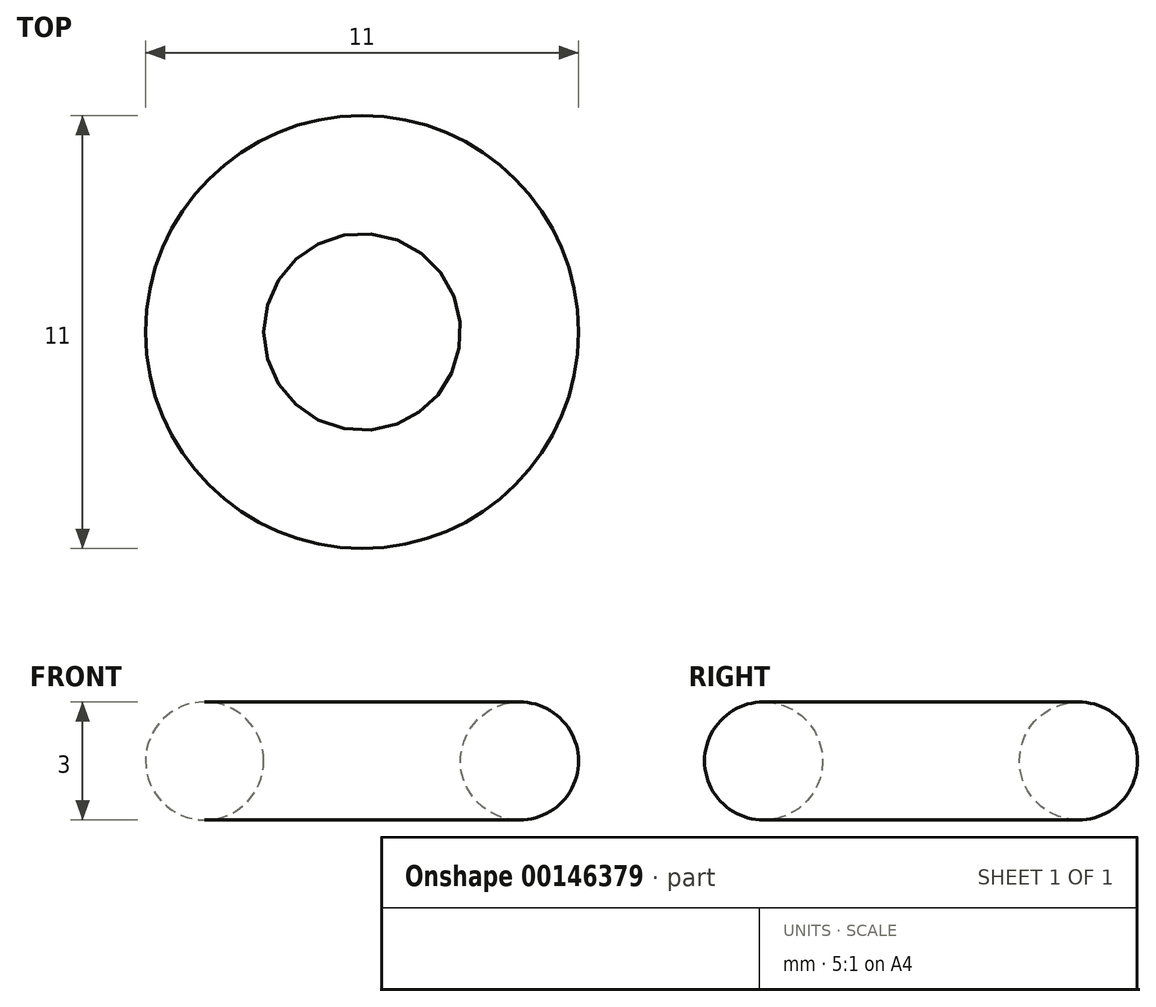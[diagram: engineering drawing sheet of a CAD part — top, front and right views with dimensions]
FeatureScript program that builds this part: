
annotation { "Feature Type Name" : "Feature", "Feature Type Description" : "" }
export const myFeature = defineFeature(function(context is Context, id is Id, definition is map)
    precondition{}
    {
        {
            var Q0;
            Q0=qCreatedBy(makeId("Front.planeOp"),FACE);
            var sketch = newSketch(context, id + "F0", { "sketchPlane" : qUnion([Q0])});
            skCircle(sketch, "E0", {"center": v(0, 0) * mm, "radius": 1.5 * mm});
            skLineSegment(sketch, "E1", {"start": v(0, 0) * mm, "end": v(4, 0) * mm});
            skPoint(sketch, "E2", {"position": v(1.5, 0) * mm});
            skLineSegment(sketch, "E3", {"start": v(4, 0) * mm, "end": v(4, -2.6) * mm});
            skLineSegment(sketch, "E4", {"start": v(4, -2.6) * mm, "end": v(4, 2.86) * mm});
            skSolve(sketch);
        }
        {
            var Q0;
            Q0=makeQuery(id+"F0.imprint","IMPRINT",FACE,{"disambiguationData":[TD([[makeQuery(id+"F0.imprint","IMPRINT",EDGE,{"derivedFrom":sQuery(id+"F0.wireOp",EDGE,"E0")}),1.0]])]});
            var Q1;
            Q1=sQuery(id+"F0.wireOp",EDGE,"E4");
            revolve(context, id + "F1", {"entities" : qUnion([Q0]), "axis" : qUnion([Q1]), "revolveType" : RevolveType.FULL});
        }
    });
